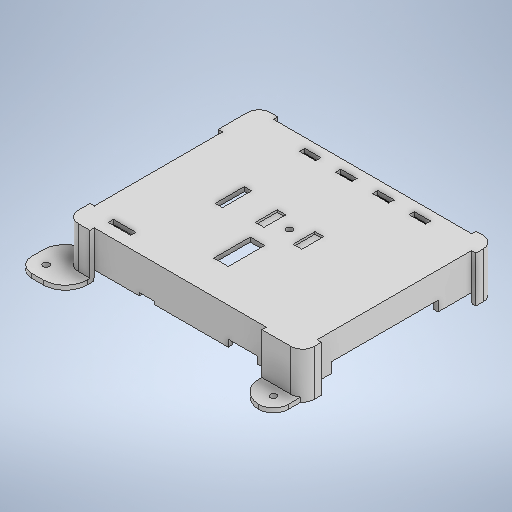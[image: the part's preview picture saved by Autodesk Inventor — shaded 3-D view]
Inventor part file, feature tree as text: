
AUTODESK INVENTOR PART (.ipt)
format: ipt  version: 2025.2 (Build 292293000, 293)  size: 641,536 bytes
history: native  units: mm
features: extrude x13, sketch x7, chamfer x6, fillet x5
ambient origin geometry x8: Origin, YZ Plane, XZ Plane, XY Plane, X Axis, Y Axis, Z Axis, Center Point
bodies: Solid1 (feature_tree)
feature tree (31):
  sketch  "Sketch1"  dims[d0=156.0mm d1=126.0mm d2=3.0mm d3=0.0mm]
  extrude  "Extrusion1"  Depth=126.0mm
  fillet  "Fillet1"  Radius=3.0mm
  extrude  "Extrusion2"  Depth=3.0mm
  extrude  "Extrusion3"  Depth=3.0mm
  fillet  "Fillet2"  Radius=3.0mm
  fillet  "Fillet3"  Radius=3.0mm
  extrude  "Extrusion4"  Depth=3.0mm
  extrude  "Extrusion5"  Depth=2.8mm
  extrude  "Extrusion6"  Depth=2.8mm
  extrude  "Extrusion7"  Depth=6.0mm
  extrude  "Extrusion8"  Depth=6.0mm
  chamfer  "Chamfer1"  Distance=6.0mm
  extrude  "Extrusion9"  Depth=6.0mm
  extrude  "Extrusion10"  Depth=6.0mm
  fillet  "Fillet4"  Radius=6.0mm
  extrude  "Extrusion11"  Depth=6.0mm
  fillet  "Fillet5"  Radius=6.0mm
  extrude  "Extrusion13"  Depth=10.0mm
  extrude  "Extrusion14"  Depth=10.0mm
  chamfer  "Chamfer2"  Distance=10.0mm
  chamfer  "Chamfer3"  Distance=10.0mm
  chamfer  "Chamfer4"  Distance=21.8mm
  chamfer  "Chamfer5"  Distance=44.0mm
  chamfer  "Chamfer6"  Distance=102.0mm
  sketch  "Sketch2"  dims[d4=5.0mm d5=3.0mm]
  sketch  "Sketch3"  dims[d6=3.0mm d7=3.0mm d8=3.0mm d9=3.0mm]
  sketch  "Sketch4"  dims[d10=3.0mm d11=3.0mm]
  sketch  "Sketch5"  dims[d12=3.0mm d13=2.8mm]
  sketch  "Sketch6"  dims[d14=2.8mm d15=2.8mm]
  sketch  "Sketch7"  dims[d16=2.8mm d17=6.0mm d18=6.0mm d19=6.0mm d20=6.0mm d21=6.0mm d22=6.0mm d23=6.0mm d24=6.0mm d25=10.0mm d26=10.0mm d27=10.0mm d28=10.0mm d29=21.8mm d30=0.0mm d31=44.0mm d32=102.0mm d33=20.0mm d34=33.0mm d35=14.25mm d36=99.75mm d37=22.0mm d38=0.0mm d39=5.0mm d40=5.0mm d41=4.3mm d42=4.3mm d43=4.3mm d44=4.3mm d45=8.0mm d46=0.0mm d47=20.0mm d48=0.0mm d49=15.0mm d50=0.0mm d51=17.0mm d52=0.0mm d53=31.0mm d54=105.0mm d55=20.0mm d56=0.0mm d57=2.8mm d58=2.0mm d59=45.0deg d60=10.0mm d61=10.0mm d62=13.0mm d63=13.0mm d64=10.0mm d65=10.0mm d66=10.0mm d67=10.0mm d68=10.0mm d69=10.0mm d70=13.0mm d71=13.0mm d72=13.0mm d73=13.0mm d74=13.0mm d75=13.0mm d76=3.0mm d77=3.0mm d78=15.0mm d79=15.0mm d80=31.5mm d81=0.0mm d82=156.0mm d83=126.0mm d84=25.0mm d85=20.0mm d86=16.0mm d87=16.0mm d88=20.0mm d89=17.0mm d90=28.0mm d91=20.0mm d92=17.0mm d93=3.0mm d94=0.0mm d95=17.0mm d96=10.0mm d97=4.3mm d98=4.3mm d99=4.3mm d100=3.0mm d101=0.0mm d102=15.0mm d103=14.5mm d104=8.0mm d105=15.5mm d106=3.6mm d107=74.0mm d108=23.0mm d109=10.0mm d110=25.0mm d111=40.0mm d112=50.0mm d113=5.0mm d114=20.0mm d115=31.6mm d116=6.5mm d117=11.1mm d118=3.6mm d119=14.05mm d120=11.1mm d121=14.3mm d122=11.1mm d123=13.7mm d128=0.0mm d129=0.0mm d130=3.6mm d131=11.1mm d132=3.6mm d133=11.1mm d134=11.1mm d135=0.0mm d136=0.0mm d137=0.0mm d138=75.0mm d139=60.0mm d140=4.3mm d141=20.0mm d142=15.0mm d143=32.0mm d144=1.5mm d145=0.0mm d146=2.0mm d147=2.0mm d148=45.0deg d149=0.3mm d150=6.5mm d151=45.0deg d152=0.3mm d153=6.5mm d154=45.0deg d155=0.3mm d156=6.5mm d157=45.0deg d158=0.3mm d159=6.5mm d160=45.0deg]
